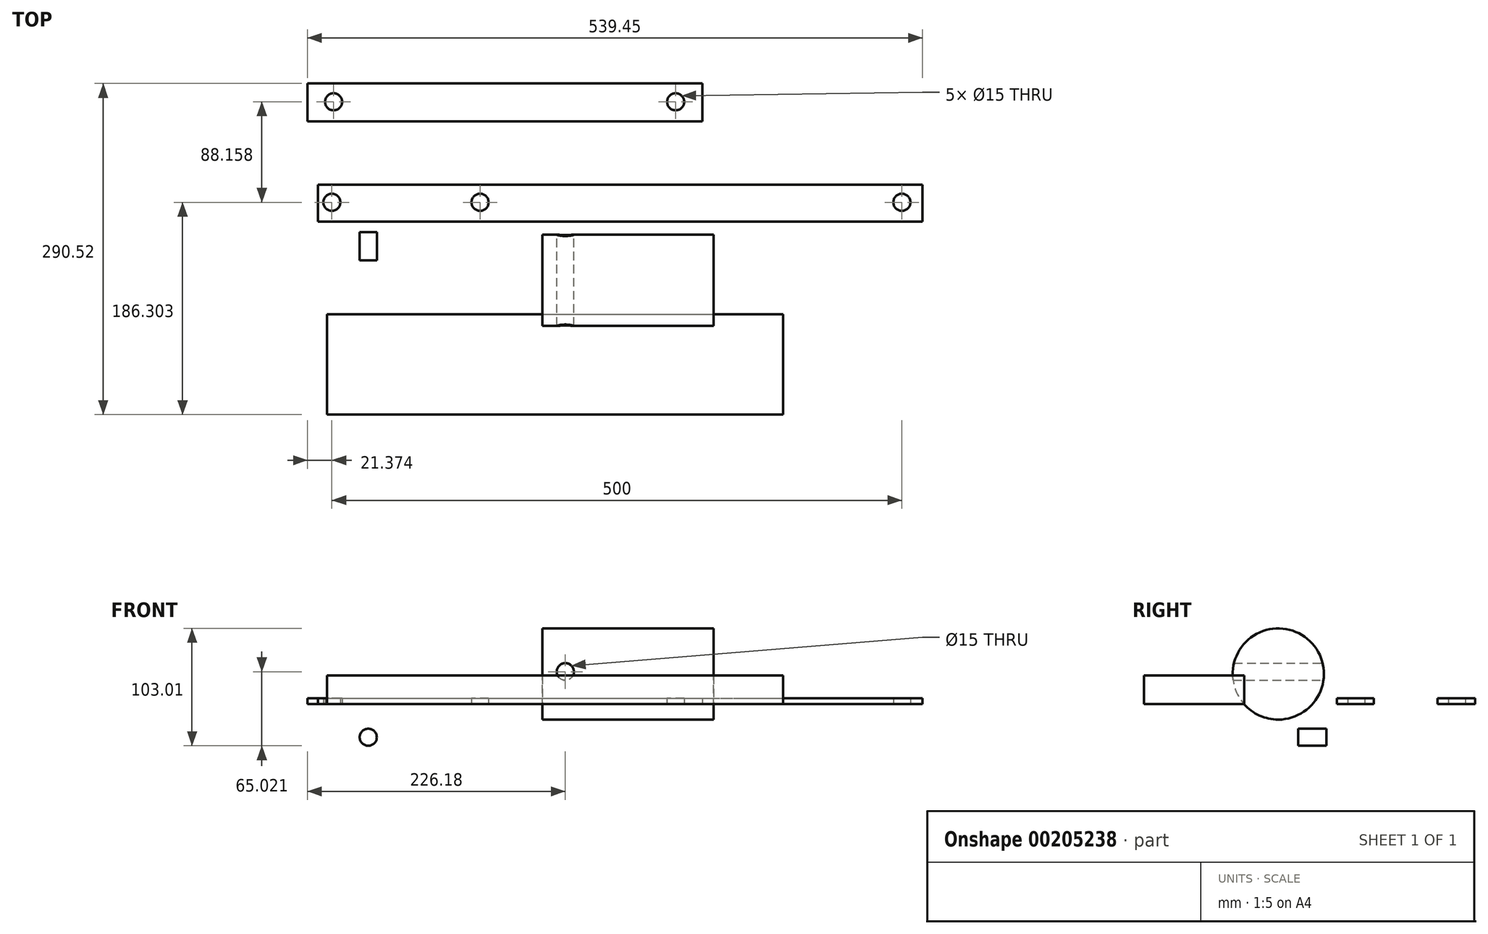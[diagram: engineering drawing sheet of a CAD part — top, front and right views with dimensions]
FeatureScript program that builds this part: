
annotation { "Feature Type Name" : "Feature", "Feature Type Description" : "" }
export const myFeature = defineFeature(function(context is Context, id is Id, definition is map)
    precondition{}
    {
        {
            var Q0;
            Q0=qCreatedBy(makeId("Right.planeOp"),FACE);
            var sketch = newSketch(context, id + "F0", { "sketchPlane" : qUnion([Q0])});
            skCircle(sketch, "E0", {"center": v(-42.35, 26.45) * mm, "radius": 40 * mm});
            skSolve(sketch);
        }
        {
            var Q0;
            Q0 = qSketchRegion(id + "F0", true);
            extrude(context, id + "F1", {"entities" : qUnion([Q0]), "depth" : 150 * mm, "offsetDistance" : 25 * mm});
        }
        {
            var Q0;
            Q0=qCreatedBy(makeId("Front.planeOp"),FACE);
            var sketch = newSketch(context, id + "F2", { "sketchPlane" : qUnion([Q0])});
            skCircle(sketch, "E1", {"center": v(20, 28.46) * mm, "radius": 7.5 * mm});
            skSolve(sketch);
        }
        {
            var Q0;
            Q0 = qSketchRegion(id + "F2", true);
            extrude(context, id + "F3", {"entities" : qUnion([Q0]), "operationType" : NewBodyOperationType.REMOVE, "endBound" : BoundingType.THROUGH_ALL, "depth" : 25 * mm, "offsetDistance" : 25 * mm});
        }
        {
            var Q0;
            Q0=qCreatedBy(makeId("Top.planeOp"),FACE);
            var sketch = newSketch(context, id + "F4", { "sketchPlane" : qUnion([Q0])});
            skCircle(sketch, "E2", {"center": v(-184.8, 26.07) * mm, "radius": 7.5 * mm});
            skCircle(sketch, "E3", {"center": v(315.2, 26.07) * mm, "radius": 7.5 * mm});
            skCircle(sketch, "E4", {"center": v(-54.8, 26.07) * mm, "radius": 7.5 * mm});
            skLineSegment(sketch, "E5.bottom", {"start": v(-197.01, 41.38) * mm, "end": v(333.27, 41.38) * mm});
            skLineSegment(sketch, "E5.top", {"start": v(-197.01, 8.99) * mm, "end": v(333.27, 8.99) * mm});
            skLineSegment(sketch, "E5.left", {"start": v(-197.01, 41.38) * mm, "end": v(-197.01, 8.99) * mm});
            skLineSegment(sketch, "E5.right", {"start": v(333.27, 41.38) * mm, "end": v(333.27, 8.99) * mm});
            skSolve(sketch);
        }
        {
            var Q0;
            Q0 = qSketchRegion(id + "F4", true);
            extrude(context, id + "F5", {"entities" : qUnion([Q0]), "depth" : 5 * mm, "offsetDistance" : 25 * mm});
        }
        {
            var Q0;
            Q0=qCreatedBy(makeId("Front.planeOp"),FACE);
            var sketch = newSketch(context, id + "F6", { "sketchPlane" : qUnion([Q0])});
            skCircle(sketch, "E6", {"center": v(-152.86, -29.06) * mm, "radius": 7.5 * mm});
            skSolve(sketch);
        }
        {
            var Q0;
            Q0 = qSketchRegion(id + "F6", true);
            extrude(context, id + "F7", {"entities" : qUnion([Q0]), "depth" : 25 * mm, "offsetDistance" : 25 * mm});
        }
        {
            var Q0;
            Q0=qCreatedBy(makeId("Top.planeOp"),FACE);
            var sketch = newSketch(context, id + "F8", { "sketchPlane" : qUnion([Q0])});
            skLineSegment(sketch, "E7.bottom", {"start": v(-189.08, -72.23) * mm, "end": v(210.92, -72.23) * mm});
            skLineSegment(sketch, "E7.top", {"start": v(-189.08, -160.23) * mm, "end": v(210.92, -160.23) * mm});
            skLineSegment(sketch, "E7.left", {"start": v(-189.08, -72.23) * mm, "end": v(-189.08, -160.23) * mm});
            skLineSegment(sketch, "E7.right", {"start": v(210.92, -72.23) * mm, "end": v(210.92, -160.23) * mm});
            skSolve(sketch);
        }
        {
            var Q0;
            Q0 = qSketchRegion(id + "F8", true);
            extrude(context, id + "F9", {"entities" : qUnion([Q0]), "depth" : 25 * mm, "offsetDistance" : 25 * mm});
        }
        {
            var Q0;
            Q0=qCreatedBy(makeId("Top.planeOp"),FACE);
            var sketch = newSketch(context, id + "F10", { "sketchPlane" : qUnion([Q0])});
            skCircle(sketch, "E8", {"center": v(-183.28, 114.23) * mm, "radius": 7.5 * mm});
            skCircle(sketch, "E9", {"center": v(116.72, 114.23) * mm, "radius": 7.5 * mm});
            skLineSegment(sketch, "E10.bottom", {"start": v(-206.18, 130.3) * mm, "end": v(140.26, 130.3) * mm});
            skLineSegment(sketch, "E10.top", {"start": v(-206.18, 97.2) * mm, "end": v(140.26, 97.2) * mm});
            skLineSegment(sketch, "E10.left", {"start": v(-206.18, 130.3) * mm, "end": v(-206.18, 97.2) * mm});
            skLineSegment(sketch, "E10.right", {"start": v(140.26, 130.3) * mm, "end": v(140.26, 97.2) * mm});
            skSolve(sketch);
        }
        {
            var Q0;
            Q0 = qSketchRegion(id + "F10", true);
            extrude(context, id + "F11", {"entities" : qUnion([Q0]), "depth" : 5 * mm, "offsetDistance" : 25 * mm});
        }
    });
